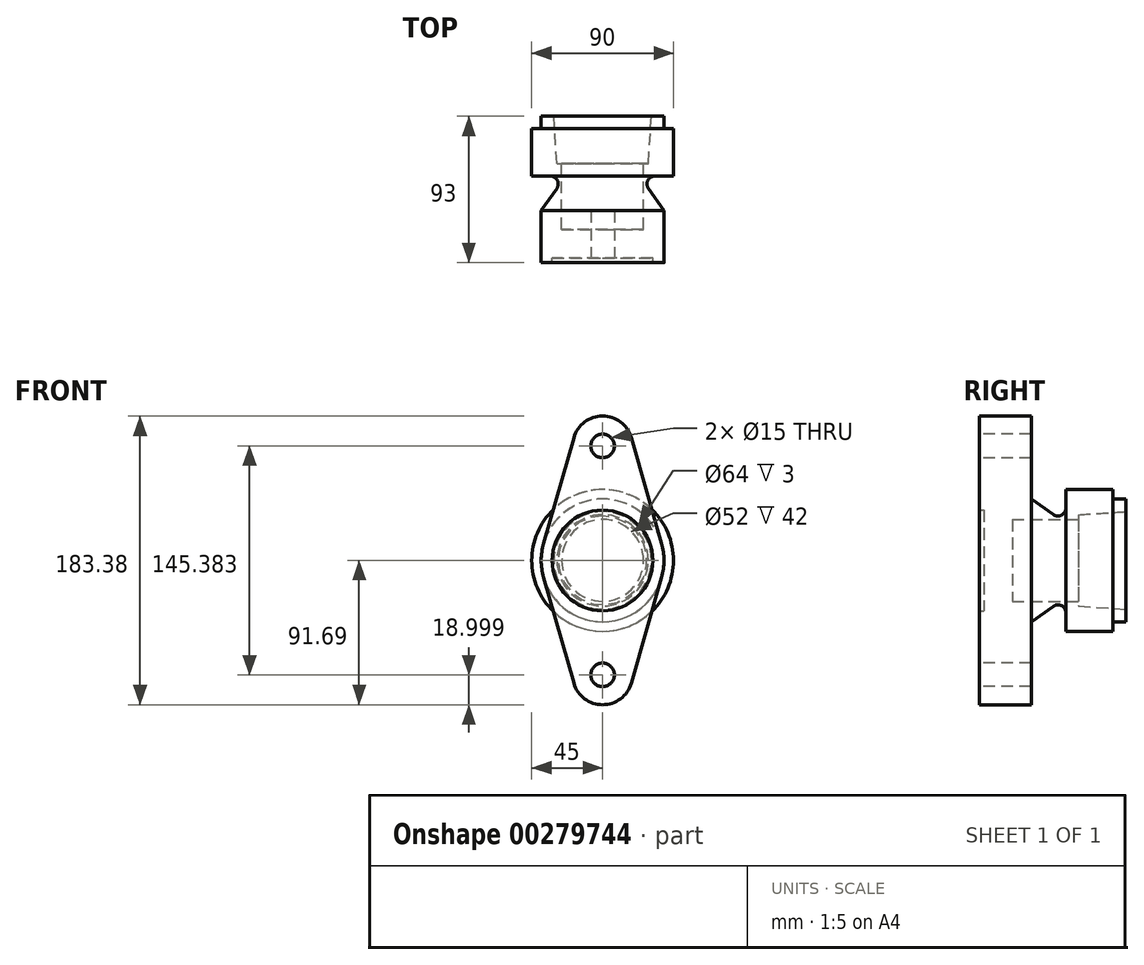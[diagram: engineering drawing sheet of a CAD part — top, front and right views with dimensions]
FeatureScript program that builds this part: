
annotation { "Feature Type Name" : "Feature", "Feature Type Description" : "" }
export const myFeature = defineFeature(function(context is Context, id is Id, definition is map)
    precondition{}
    {
        {
            var Q0;
            Q0=qCreatedBy(makeId("Right.planeOp"),FACE);
            var sketch = newSketch(context, id + "F0", { "sketchPlane" : qUnion([Q0])});
            skLineSegment(sketch, "E0", {"start": v(3, 0) * mm, "end": v(3, 32) * mm});
            skLineSegment(sketch, "E1", {"start": v(3, 32) * mm, "end": v(0, 32) * mm});
            skLineSegment(sketch, "E2", {"start": v(0, 32) * mm, "end": v(0, 39) * mm});
            skLineSegment(sketch, "E3", {"start": v(0, 39) * mm, "end": v(33, 39) * mm});
            skLineSegment(sketch, "E4", {"start": v(33, 39) * mm, "end": v(47.13, 29.1) * mm});
            skLineSegment(sketch, "E5", {"start": v(55, 33.2) * mm, "end": v(55, 45) * mm});
            skLineSegment(sketch, "E6", {"start": v(55, 45) * mm, "end": v(85, 45) * mm});
            skLineSegment(sketch, "E7", {"start": v(85, 45) * mm, "end": v(85, 39) * mm});
            skLineSegment(sketch, "E8", {"start": v(85, 39) * mm, "end": v(93, 39) * mm});
            skLineSegment(sketch, "E9", {"start": v(93, 39) * mm, "end": v(93, 31) * mm});
            skLineSegment(sketch, "E10", {"start": v(93, 31) * mm, "end": v(63, 29) * mm});
            skLineSegment(sketch, "E11", {"start": v(63, 29) * mm, "end": v(63, 26) * mm});
            skLineSegment(sketch, "E12", {"start": v(63, 26) * mm, "end": v(21, 26) * mm});
            skLineSegment(sketch, "E13", {"start": v(21, 26) * mm, "end": v(21, 0) * mm});
            skLineSegment(sketch, "E14", {"start": v(21, 0) * mm, "end": v(3, 0) * mm});
            skPoint(sketch, "E15.visualSharp", {"position": v(55, 23.6) * mm});
            skArc(sketch, "E15.filletArc", {"start": v(47.13, 29.1) * mm, "mid": v(52.3, 28.77) * mm, "end": v(55, 33.2) * mm});
            skSolve(sketch);
        }
        {
            var Q0;
            Q0 = qSketchRegion(id + "F0", true);
            var Q1;
            Q1=sQuery(id+"F0.wireOp",EDGE,"E14");
            revolve(context, id + "F1", {"entities" : qUnion([Q0]), "axis" : qUnion([Q1]), "revolveType" : RevolveType.FULL});
        }
        {
            var Q0;
            Q0=qCreatedBy(makeId("Front.planeOp"),FACE);
            var sketch = newSketch(context, id + "F2", { "sketchPlane" : qUnion([Q0])});
            skLineSegment(sketch, "E16", {"start": v(0, 0) * mm, "end": v(0, 150) * mm, "construction": true});
            skLineSegment(sketch, "E17", {"start": v(0, 72.7) * mm, "end": v(70, 72.7) * mm, "construction": true});
            skLineSegment(sketch, "E18", {"start": v(0, 72.7) * mm, "end": v(-66.14, 72.7) * mm, "construction": true});
            skCircle(sketch, "E19", {"center": v(0, 72.7) * mm, "radius": 7.5 * mm});
            skArc(sketch, "E20", {"start": v(18.27, 77.92) * mm, "mid": v(0, 91.7) * mm, "end": v(-18.27, 77.92) * mm});
            skArc(sketch, "E21", {"start": v(-37.5, -10.73) * mm, "mid": v(0, -39) * mm, "end": v(37.5, -10.73) * mm});
            skPoint(sketch, "E22.end.orphan", {"position": v(-40.7, 0) * mm});
            skPoint(sketch, "E23.end.orphan", {"position": v(40.7, 0) * mm});
            skLineSegment(sketch, "E24", {"start": v(-18.27, 77.92) * mm, "end": v(-37.5, 10.73) * mm});
            skLineSegment(sketch, "E25", {"start": v(37.5, 10.73) * mm, "end": v(18.27, 77.92) * mm});
            skLineSegment(sketch, "E26.MirrorCS", {"start": v(-18.27, -77.92) * mm, "end": v(-37.5, -10.73) * mm});
            skLineSegment(sketch, "E27.MirrorCS", {"start": v(37.5, -10.73) * mm, "end": v(18.27, -77.92) * mm});
            skCircle(sketch, "E28.MirrorC", {"center": v(0, -72.7) * mm, "radius": 7.5 * mm});
            skArc(sketch, "E29.MirrorCS", {"start": v(18.27, -77.92) * mm, "mid": v(0, -91.7) * mm, "end": v(-18.27, -77.92) * mm});
            skArc(sketch, "E30.trimOffspring", {"start": v(37.5, 10.73) * mm, "mid": v(0, 39) * mm, "end": v(-37.5, 10.73) * mm});
            skSolve(sketch);
        }
        {
            var Q0;
            Q0=makeQuery(id+"F2.imprint","IMPRINT",FACE,{"disambiguationData":[TD([[makeQuery(id+"F2.imprint","IMPRINT",EDGE,{"derivedFrom":sQuery(id+"F2.wireOp",EDGE,"E19")}),-1.0]])]});
            var Q1;
            Q1=makeQuery(id+"F2.imprint","IMPRINT",FACE,{"disambiguationData":[TD([[makeQuery(id+"F2.imprint","IMPRINT",EDGE,{"derivedFrom":sQuery(id+"F2.wireOp",EDGE,"E21")}),-1.0]])]});
            extrude(context, id + "F3", {"entities" : qUnion([Q0, Q1]), "operationType" : NewBodyOperationType.ADD, "oppositeDirection" : true, "depth" : 33 * mm});
        }
    });
